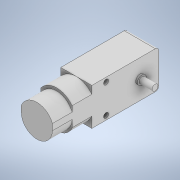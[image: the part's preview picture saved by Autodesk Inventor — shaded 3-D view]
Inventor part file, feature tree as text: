
AUTODESK INVENTOR PART (.ipt)
format: ipt  version: 2020 (Build 240168000, 168)  size: 192,512 bytes
history: native  units: mm
features: extrude x8, sketch x8, other x2, fillet x2, mirror x1
ambient origin geometry x8: Origin, YZ Plane, XZ Plane, XY Plane, X Axis, Y Axis, Z Axis, Center Point
bodies: Body1 (feature_tree)
feature tree (21):
  other  "Sólido1"
  extrude  "Extrusão1"  Depth=22.5mm
  extrude  "Extrusão2"  Depth=64.2mm
  extrude  "Extrusão3"  Depth=1.1mm
  other  "Plano de trabalho1"
  mirror  "Espelhamento1"
  fillet  "Arredondamento1"  Radius=1.1mm
  fillet  "Arredondamento2"  Radius=3.6mm
  extrude  "Extrusão4"  [1 undecoded]
  extrude  "Extrusão5"  Depth=2.0mm
  extrude  "Extrusão6"  Depth=2.5mm
  extrude  "Extrusão7"  Depth=17.5mm
  extrude  "Extrusão8"  TaperAngle=0.0deg  [1 undecoded]
  sketch  "Esboço1"  dims[d0=18.8mm d1=22.5mm]
  sketch  "Esboço2"  dims[d2=64.2mm d3=0.0mm d4=11.25mm]
  sketch  "Esboço3"  dims[d5=11.2mm d6=5.4mm d7=1.1mm d8=0.0mm d9=3.6mm]
  sketch  "Esboço4"  dims[d10=7.9mm d11=0.0mm d12=-9.4mm]
  sketch  "Esboço5"  dims[d13=2.0mm d14=2.0mm]
  sketch  "Esboço6"  dims[d15=31.8mm d16=2.5mm]
  sketch  "Esboço7"  dims[d17=3.0mm d18=17.5mm]
  sketch  "Esboço9"  dims[d19=3.0mm d20=0.0mm d21=0.0mm d22=23.8mm d23=0.0mm d24=23.8mm d25=0.0mm d26=11.9mm d27=0.0mm d29=11.9mm d30=0.0mm]
note: 2 required parameter values undecoded (feature->parameter linkage not recoverable at this tier; creation-order binding heuristic only, values carry confidence <= 0.55)
